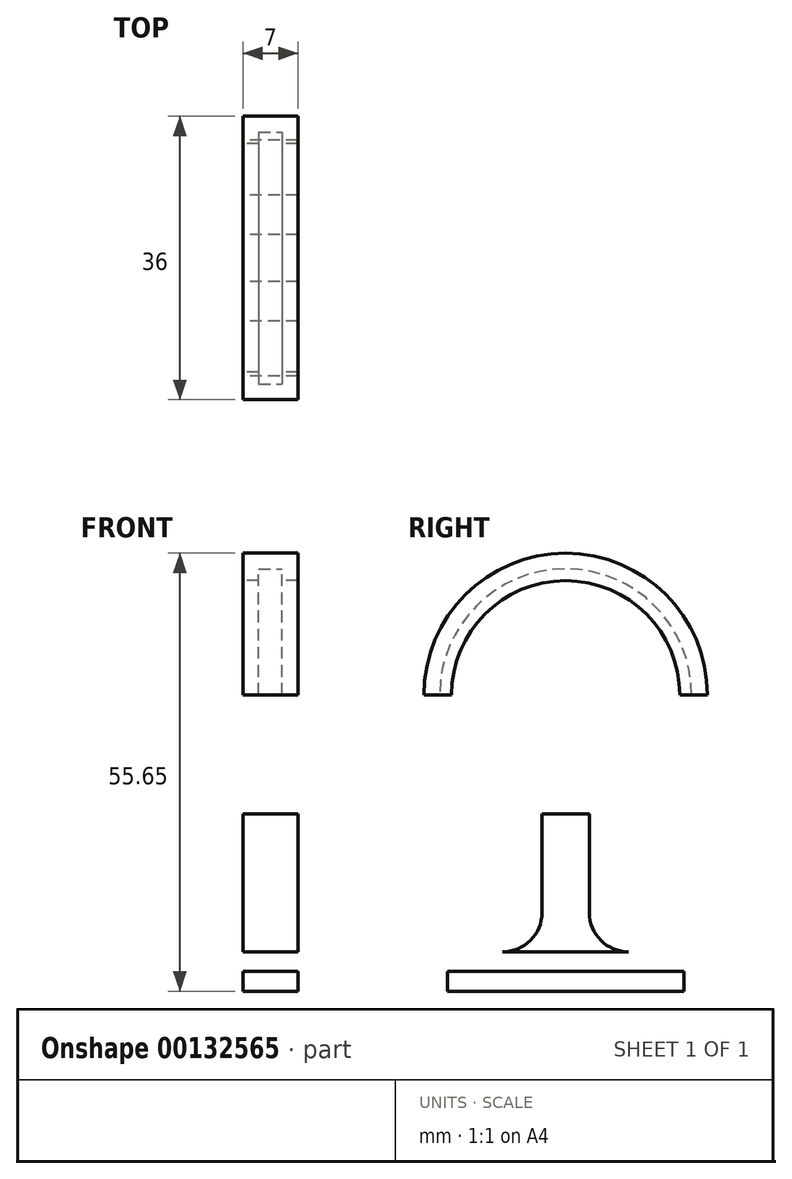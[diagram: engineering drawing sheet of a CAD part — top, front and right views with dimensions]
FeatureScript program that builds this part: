
annotation { "Feature Type Name" : "Feature", "Feature Type Description" : "" }
export const myFeature = defineFeature(function(context is Context, id is Id, definition is map)
    precondition{}
    {
        {
            var Q0;
            Q0=qCreatedBy(makeId("Right.planeOp"),FACE);
            var sketch = newSketch(context, id + "F0", { "sketchPlane" : qUnion([Q0])});
            skCircle(sketch, "E0", {"center": v(0, 0) * mm, "radius": 16 * mm});
            skCircle(sketch, "E1", {"center": v(0, 0) * mm, "radius": 18 * mm});
            skLineSegment(sketch, "E2", {"start": v(18, 0) * mm, "end": v(-18, 0) * mm});
            skCircle(sketch, "E3", {"center": v(0, 0) * mm, "radius": 14.5 * mm});
            skSolve(sketch);
        }
        {
            var Q0;
            {var subQ0=sQuery(id+"F0.wireOp",EDGE,"E2");var subQ1=sQuery(id+"F0.wireOp",EDGE,"E0");var subQ2=makeQuery(id+"F0.imprint","INTERSECT",VERTEX,{"disambiguationData":[OD(0.0)],"derivedFrom":[subQ1,subQ0]});Q0=makeQuery(id+"F0.imprint","IMPRINT",FACE,{"disambiguationData":[TD([[makeQuery(id+"F0.imprint","IMPRINT",EDGE,{"disambiguationData":[TD([[subQ2,1.0]])],"derivedFrom":subQ1}),1.0]])]});}
            var Q1;
            {var subQ0=sQuery(id+"F0.wireOp",EDGE,"E2");var subQ1=sQuery(id+"F0.wireOp",EDGE,"E0");var subQ2=makeQuery(id+"F0.imprint","INTERSECT",VERTEX,{"disambiguationData":[OD(0.0)],"derivedFrom":[subQ1,subQ0]});Q1=makeQuery(id+"F0.imprint","IMPRINT",FACE,{"disambiguationData":[TD([[makeQuery(id+"F0.imprint","IMPRINT",EDGE,{"disambiguationData":[TD([[subQ2,1.0]])],"derivedFrom":subQ1}),-1.0]])]});}
            extrude(context, id + "F1", {"entities" : qUnion([Q0, Q1]), "endBound" : BoundingType.SYMMETRIC, "depth" : 7 * mm});
        }
        {
            var Q0;
            {var subQ0=sQuery(id+"F0.wireOp",EDGE,"E2");var subQ1=sQuery(id+"F0.wireOp",EDGE,"E0");var subQ2=makeQuery(id+"F0.imprint","INTERSECT",VERTEX,{"disambiguationData":[OD(0.0)],"derivedFrom":[subQ1,subQ0]});Q0=makeQuery(id+"F0.imprint","IMPRINT",FACE,{"disambiguationData":[TD([[makeQuery(id+"F0.imprint","IMPRINT",EDGE,{"disambiguationData":[TD([[subQ2,1.0]])],"derivedFrom":subQ1}),1.0]])]});}
            extrude(context, id + "F2", {"entities" : qUnion([Q0]), "operationType" : NewBodyOperationType.REMOVE, "endBound" : BoundingType.SYMMETRIC, "oppositeDirection" : true, "depth" : 3 * mm});
        }
        {
            var Q0;
            Q0=qCreatedBy(makeId("Right.planeOp"),FACE);
            var sketch = newSketch(context, id + "F3", { "sketchPlane" : qUnion([Q0])});
            skLineSegment(sketch, "E4.bottom", {"start": v(-3, -15.15) * mm, "end": v(3, -15.15) * mm});
            skLineSegment(sketch, "E4.top", {"start": v(-3, -35.15) * mm, "end": v(3, -35.15) * mm});
            skLineSegment(sketch, "E4.left", {"start": v(-3, -15.15) * mm, "end": v(-3, -27.65) * mm});
            skLineSegment(sketch, "E4.right", {"start": v(3, -15.15) * mm, "end": v(3, -27.65) * mm});
            skPoint(sketch, "E4.middle", {"position": v(0, -25.15) * mm});
            skLineSegment(sketch, "E5.bottom", {"start": v(10, -32.65) * mm, "end": v(8, -32.65) * mm});
            skLineSegment(sketch, "E5.top", {"start": v(10, -37.65) * mm, "end": v(-10, -37.65) * mm});
            skPoint(sketch, "E5.middle", {"position": v(0, -35.15) * mm});
            skPoint(sketch, "E6.newPointA", {"position": v(-10, -32.65) * mm});
            skArc(sketch, "E6.filletArc", {"start": v(3, -27.65) * mm, "mid": v(4.46, -31.19) * mm, "end": v(8, -32.65) * mm});
            skLineSegment(sketch, "E7", {"start": v(-10, -32.65) * mm, "end": v(-8, -32.65) * mm});
            skArc(sketch, "E8.filletArc", {"start": v(-8, -32.65) * mm, "mid": v(-4.46, -31.19) * mm, "end": v(-3, -27.65) * mm});
            skLineSegment(sketch, "E9.bottom", {"start": v(-15, -32.65) * mm, "end": v(15, -32.65) * mm});
            skLineSegment(sketch, "E9.top", {"start": v(-15, -37.65) * mm, "end": v(15, -37.65) * mm});
            skLineSegment(sketch, "E9.left", {"start": v(-15, -32.65) * mm, "end": v(-15, -37.65) * mm});
            skLineSegment(sketch, "E9.right", {"start": v(15, -32.65) * mm, "end": v(15, -37.65) * mm});
            skLineSegment(sketch, "E10.bottom", {"start": v(-15, -35.15) * mm, "end": v(15, -35.15) * mm});
            skLineSegment(sketch, "E10.left", {"start": v(-15, -35.15) * mm, "end": v(-15, -37.65) * mm});
            skLineSegment(sketch, "E10.right", {"start": v(15, -35.15) * mm, "end": v(15, -37.65) * mm});
            skSolve(sketch);
        }
        {
            var Q0;
            {var subQ5=sQuery(id+"F3.wireOp",EDGE,"E9.left");Q0=makeQuery(id+"F3.imprint","IMPRINT",FACE,{"disambiguationData":[TD([[makeQuery(id+"F3.imprint","IMPRINT",EDGE,{"derivedFrom":subQ5}),1.0]])]});}
            var Q1;
            Q1=makeQuery(id+"F3.imprint","IMPRINT",FACE,{"disambiguationData":[TD([[makeQuery(id+"F3.imprint","IMPRINT",EDGE,{"derivedFrom":sQuery(id+"F3.wireOp",EDGE,"E4.bottom")}),-1.0]])]});
            extrude(context, id + "F4", {"entities" : qUnion([Q0, Q1]), "operationType" : NewBodyOperationType.ADD, "endBound" : BoundingType.SYMMETRIC, "depth" : 7 * mm});
        }
    });
